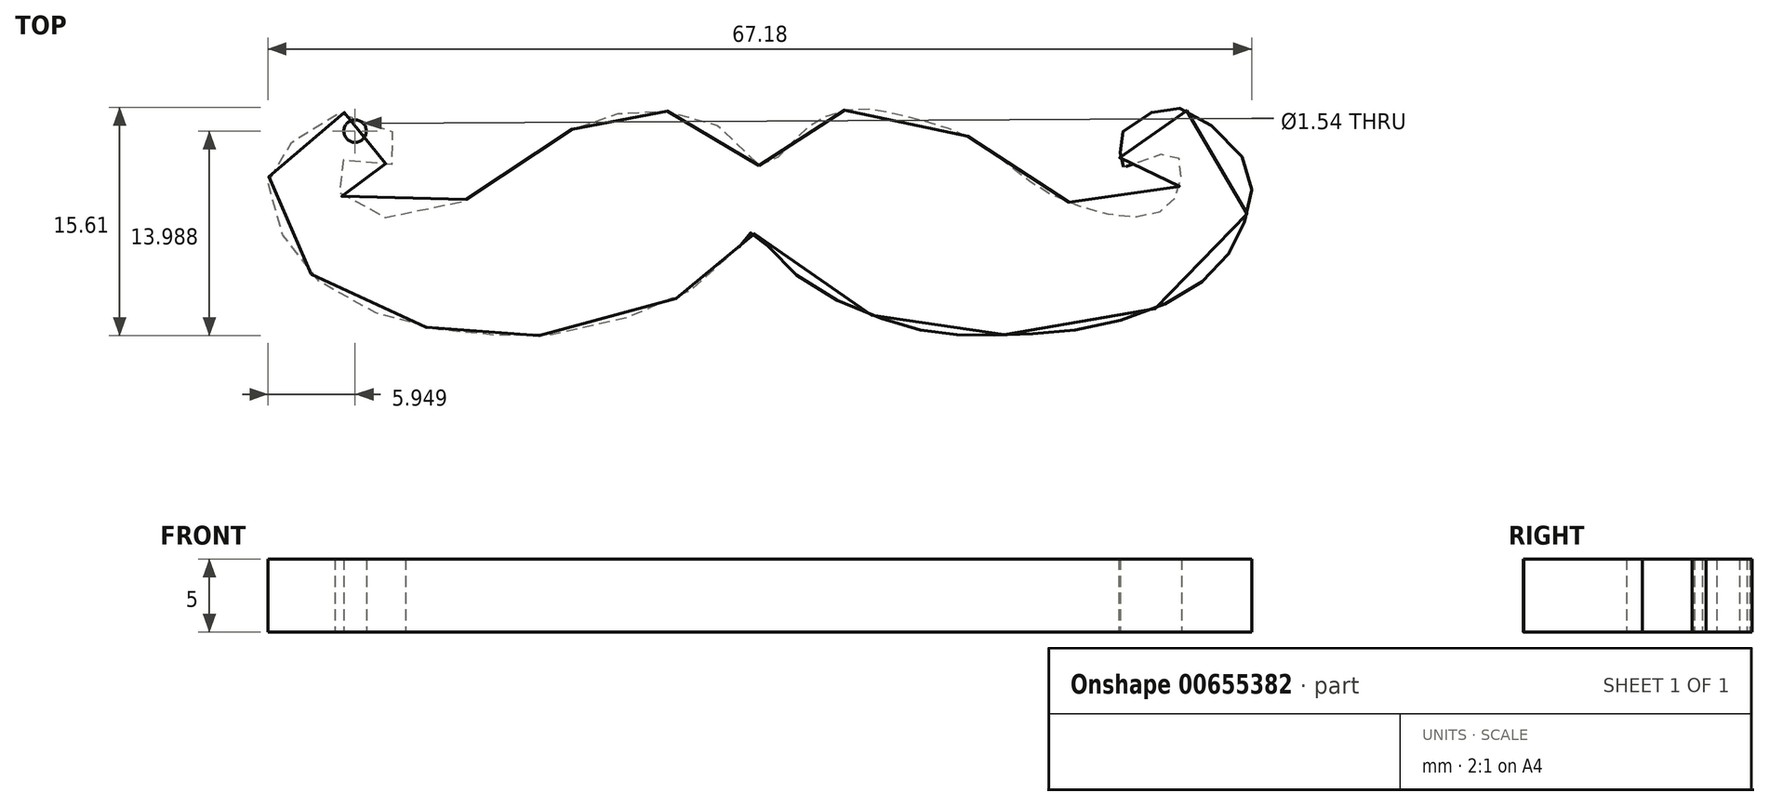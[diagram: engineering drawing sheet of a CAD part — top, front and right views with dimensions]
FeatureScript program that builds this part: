
annotation { "Feature Type Name" : "Feature", "Feature Type Description" : "" }
export const myFeature = defineFeature(function(context is Context, id is Id, definition is map)
    precondition{}
    {
        {
            var Q0;
            Q0=qCreatedBy(makeId("Top.planeOp"),FACE);
            var sketch = newSketch(context, id + "F0", { "sketchPlane" : qUnion([Q0])});
            skFitSpline(sketch, "E0", {"points": [v(-38.63, 19.84) * mm, v(-36.17, 21.6) * mm, v(-34.68, 22.9) * mm, v(-32.13, 23.73) * mm, v(-28.56, 23.2) * mm, v(-24.42, 21.86) * mm, v(-21.54, 19.86) * mm, v(-18.97, 18.03) * mm, v(-14.04, 16.4) * mm, v(-10.72, 17.01) * mm, v(-9.79, 19.23) * mm, v(-10.47, 20.65) * mm, v(-13.98, 19.74) * mm, v(-13.98, 20.58) * mm, v(-13.98, 21.84) * mm, v(-11.41, 23.64) * mm, v(-9.1, 23.43) * mm, v(-5.37, 19.95) * mm, v(-5.22, 16.82) * mm, v(-6.74, 13.57) * mm, v(-10.57, 10.52) * mm, v(-16.76, 8.64) * mm, v(-21.75, 8.27) * mm, v(-25.84, 8.32) * mm, v(-30.24, 9.35) * mm, v(-36.11, 12.4) * mm, v(-38.8, 15.09) * mm, v(-39.32, 15.2) * mm, v(-40.06, 14.2) * mm, v(-43, 11.52) * mm, v(-46.88, 9.68) * mm, v(-52.44, 8.32) * mm, v(-55.27, 8.22) * mm, v(-58.47, 8.32) * mm, v(-61.9, 8.92) * mm, v(-65.84, 10.18) * mm, v(-69.02, 12.22) * mm, v(-71.03, 14.82) * mm, v(-72.13, 18) * mm, v(-72, 19.37) * mm, v(-70.55, 21.42) * mm, v(-67.85, 23.27) * mm, v(-66.08, 23.31) * mm, v(-62.92, 21.32) * mm, v(-63.2, 19.93) * mm, v(-65.72, 20.4) * mm, v(-67.2, 20.1) * mm, v(-67.6, 19.49) * mm, v(-67.17, 17.79) * mm, v(-65.26, 16.44) * mm, v(-59.96, 16.95) * mm, v(-55.67, 19.45) * mm, v(-52.64, 21.6) * mm, v(-50.23, 22.85) * mm, v(-47.95, 23.44) * mm, v(-46.08, 23.67) * mm, v(-42.9, 23.15) * mm, v(-40.97, 22.14) * mm, v(-38.63, 19.84) * mm]});
            skCircle(sketch, "E1", {"center": v(-66.22, 22.19) * mm, "radius": 0.77 * mm});
            skSolve(sketch);
        }
        {
            var Q0;
            Q0 = qSketchRegion(id + "F0", true);
            extrude(context, id + "F1", {"entities" : qUnion([Q0]), "depth" : 5 * mm, "offsetDistance" : 25.4 * mm});
        }
        {
            var Q0;
            Q0 = qSketchRegion(id + "F0", true);
            extrude(context, id + "F2", {"entities" : qUnion([Q0]), "operationType" : NewBodyOperationType.REMOVE, "oppositeDirection" : true, "depth" : 5 * mm, "offsetDistance" : 25 * mm});
        }
    });
